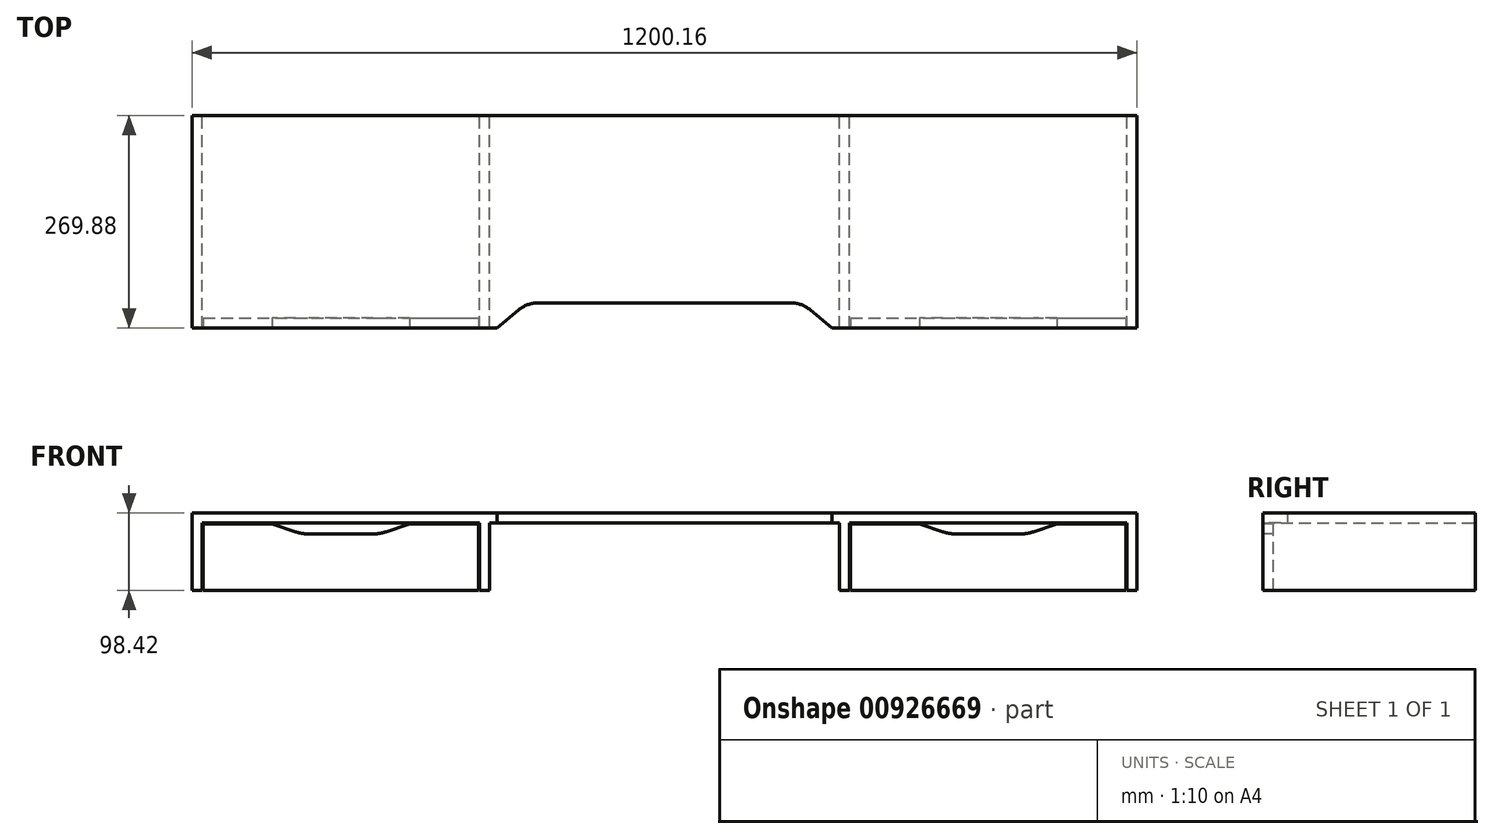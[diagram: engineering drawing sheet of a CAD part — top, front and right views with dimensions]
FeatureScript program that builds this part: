
annotation { "Feature Type Name" : "Feature", "Feature Type Description" : "" }
export const myFeature = defineFeature(function(context is Context, id is Id, definition is map)
    precondition{}
    {
        {
            var Q0;
            Q0=qCreatedBy(makeId("Top.planeOp"),FACE);
            var sketch = newSketch(context, id + "F0", { "sketchPlane" : qUnion([Q0])});
            skLineSegment(sketch, "E0.bottom", {"start": v(600.08, -134.94) * mm, "end": v(-600.08, -134.94) * mm});
            skLineSegment(sketch, "E0.top", {"start": v(600.08, 134.94) * mm, "end": v(-600.08, 134.94) * mm});
            skLineSegment(sketch, "E0.left", {"start": v(600.08, -134.94) * mm, "end": v(600.08, 134.94) * mm});
            skLineSegment(sketch, "E0.right", {"start": v(-600.08, -134.94) * mm, "end": v(-600.08, 134.94) * mm});
            skPoint(sketch, "E0.middle", {"position": v(0, 0) * mm});
            skSolve(sketch);
        }
        {
            var Q0;
            Q0 = qSketchRegion(id + "F0", true);
            extrude(context, id + "F1", {"entities" : qUnion([Q0]), "depth" : 12.7 * mm, "offsetDistance" : 25.4 * mm});
        }
        {
            var Q0;
            Q0=makeQuery(id+"F1.opExtrude","SWEPT_FACE",FACE,{"disambiguationData":[OSD([sQuery(id+"F0.wireOp",EDGE,"E0.left")])]});
            var sketch = newSketch(context, id + "F2", { "sketchPlane" : qUnion([Q0])});
            skLineSegment(sketch, "E1.bottom", {"start": v(-134.94, 0) * mm, "end": v(134.94, 0) * mm});
            skLineSegment(sketch, "E1.top", {"start": v(-134.94, -85.73) * mm, "end": v(134.94, -85.73) * mm});
            skLineSegment(sketch, "E1.left", {"start": v(-134.94, 0) * mm, "end": v(-134.94, -85.73) * mm});
            skLineSegment(sketch, "E1.right", {"start": v(134.94, 0) * mm, "end": v(134.94, -85.73) * mm});
            skSolve(sketch);
        }
        {
            var Q0;
            Q0 = qSketchRegion(id + "F2", true);
            extrude(context, id + "F3", {"entities" : qUnion([Q0]), "operationType" : NewBodyOperationType.ADD, "depth" : -12.7 * mm, "offsetDistance" : 25.4 * mm});
        }
        {
            var Q0;
            Q0=makeQuery(id+"F1.opExtrude","SWEPT_FACE",FACE,{"disambiguationData":[OSD([sQuery(id+"F0.wireOp",EDGE,"E0.right")])]});
            var sketch = newSketch(context, id + "F4", { "sketchPlane" : qUnion([Q0])});
            skLineSegment(sketch, "E2.bottom", {"start": v(-134.94, 0) * mm, "end": v(134.94, 0) * mm});
            skLineSegment(sketch, "E2.top", {"start": v(-134.94, -85.73) * mm, "end": v(134.94, -85.73) * mm});
            skLineSegment(sketch, "E2.left", {"start": v(-134.94, 0) * mm, "end": v(-134.94, -85.72) * mm});
            skLineSegment(sketch, "E2.right", {"start": v(134.94, 0) * mm, "end": v(134.94, -85.73) * mm});
            skSolve(sketch);
        }
        {
            var Q0;
            Q0 = qSketchRegion(id + "F4", true);
            extrude(context, id + "F5", {"entities" : qUnion([Q0]), "operationType" : NewBodyOperationType.ADD, "depth" : -12.7 * mm, "offsetDistance" : 25.4 * mm});
        }
        {
            var Q0;
            Q0=makeQuery(id+"F1.opExtrude","CAP_FACE",FACE,{"disambiguationData":[OSD([sQuery(id+"F0.wireOp",EDGE,"E0.bottom"),sQuery(id+"F0.wireOp",EDGE,"E0.top"),sQuery(id+"F0.wireOp",EDGE,"E0.left"),sQuery(id+"F0.wireOp",EDGE,"E0.right")])],"isStart":true});
            var sketch = newSketch(context, id + "F6", { "sketchPlane" : qUnion([Q0])});
            skLineSegment(sketch, "E3.bottom", {"start": v(222.25, 134.94) * mm, "end": v(234.95, 134.94) * mm});
            skLineSegment(sketch, "E3.top", {"start": v(222.25, -134.94) * mm, "end": v(234.95, -134.94) * mm});
            skLineSegment(sketch, "E3.left", {"start": v(222.25, 134.94) * mm, "end": v(222.25, -134.94) * mm});
            skLineSegment(sketch, "E3.right", {"start": v(234.95, 134.94) * mm, "end": v(234.95, -134.94) * mm});
            skLineSegment(sketch, "E4.bottom", {"start": v(-234.95, 134.94) * mm, "end": v(-222.25, 134.94) * mm});
            skLineSegment(sketch, "E4.top", {"start": v(-234.95, -134.94) * mm, "end": v(-222.25, -134.94) * mm});
            skLineSegment(sketch, "E4.left", {"start": v(-234.95, 134.94) * mm, "end": v(-234.95, -134.94) * mm});
            skLineSegment(sketch, "E4.right", {"start": v(-222.25, 134.94) * mm, "end": v(-222.25, -134.94) * mm});
            skSolve(sketch);
        }
        {
            var Q0;
            Q0 = qSketchRegion(id + "F6", true);
            extrude(context, id + "F7", {"entities" : qUnion([Q0]), "operationType" : NewBodyOperationType.ADD, "depth" : 85.72 * mm, "offsetDistance" : 25.4 * mm});
        }
        {
            var Q0;
            Q0=makeQuery(id+"F1.opExtrude","CAP_FACE",FACE,{"disambiguationData":[OSD([sQuery(id+"F0.wireOp",EDGE,"E0.bottom"),sQuery(id+"F0.wireOp",EDGE,"E0.top"),sQuery(id+"F0.wireOp",EDGE,"E0.left"),sQuery(id+"F0.wireOp",EDGE,"E0.right")])],"isStart":false});
            var sketch = newSketch(context, id + "F8", { "sketchPlane" : qUnion([Q0])});
            skLineSegment(sketch, "E5", {"start": v(-174.63, -103.19) * mm, "end": v(174.63, -103.19) * mm});
            skLineSegment(sketch, "E6", {"start": v(174.62, -103.19) * mm, "end": v(212.72, -134.94) * mm});
            skLineSegment(sketch, "E7", {"start": v(-174.63, -103.19) * mm, "end": v(-212.73, -134.94) * mm});
            skLineSegment(sketch, "E8", {"start": v(-212.72, -134.94) * mm, "end": v(212.73, -134.94) * mm});
            skSolve(sketch);
        }
        {
            var Q0;
            Q0=makeQuery(id+"F8.imprint","IMPRINT",FACE,{"disambiguationData":[TD([[makeQuery(id+"F8.imprint","IMPRINT",EDGE,{"derivedFrom":sQuery(id+"F8.wireOp",EDGE,"E5")}),-1.0]])]});
            extrude(context, id + "F9", {"entities" : qUnion([Q0]), "operationType" : NewBodyOperationType.REMOVE, "oppositeDirection" : true, "depth" : 12.7 * mm, "offsetDistance" : 25.4 * mm});
        }
        {
            var Q0;
            Q0=makeQuery(id+"F9.boolean.opBoolean","COPY",EDGE,{"derivedFrom":makeQuery(id+"F9.opExtrude","SWEPT_EDGE",EDGE,{"disambiguationData":[OSD([sQuery(id+"F8.wireOp",EDGE,"E5"),sQuery(id+"F8.wireOp",EDGE,"E7")])]})});
            var Q1;
            Q1=makeQuery(id+"F9.boolean.opBoolean","COPY",EDGE,{"derivedFrom":makeQuery(id+"F9.opExtrude","SWEPT_EDGE",EDGE,{"disambiguationData":[OSD([sQuery(id+"F0.wireOp",EDGE,"E0.bottom"),sQuery(id+"F8.wireOp",EDGE,"E7"),sQuery(id+"F8.wireOp",EDGE,"E8")])]})});
            var Q2;
            Q2=makeQuery(id+"F9.boolean.opBoolean","COPY",EDGE,{"derivedFrom":makeQuery(id+"F9.opExtrude","SWEPT_EDGE",EDGE,{"disambiguationData":[OSD([sQuery(id+"F8.wireOp",EDGE,"E5"),sQuery(id+"F8.wireOp",EDGE,"E6")])]})});
            var Q3;
            Q3=makeQuery(id+"F9.boolean.opBoolean","COPY",EDGE,{"derivedFrom":makeQuery(id+"F9.opExtrude","SWEPT_EDGE",EDGE,{"disambiguationData":[OSD([sQuery(id+"F0.wireOp",EDGE,"E0.bottom"),sQuery(id+"F8.wireOp",EDGE,"E6"),sQuery(id+"F8.wireOp",EDGE,"E8")])]})});
            fillet(context, id + "F10", {"entities" : qUnion([Q0, Q1, Q2, Q3]), "radius" : 38.1 * mm, "tangentPropagation" : true, "allowEdgeOverflow" : false});
        }
        {
            var Q0;
            {var subQ0=sQuery(id+"F4.wireOp",EDGE,"E2.right");var subQ4=sQuery(id+"F0.wireOp",EDGE,"E0.right");var subQ7=sQuery(id+"F0.wireOp",EDGE,"E0.bottom");var subQ10=sQuery(id+"F6.wireOp",EDGE,"E4.bottom");Q0=makeQuery(id+"F9.boolean.opBoolean","SPLIT",FACE,{"disambiguationData":[TD([makeQuery(id+"F1.opExtrude","SWEPT_FACE",FACE,{"disambiguationData":[OSD([subQ4])]})])],"derivedFrom":makeQuery(id+"F7.boolean.opBoolean","MERGE",FACE,{"derivedFrom":[makeQuery(id+"F5.boolean.opBoolean","MERGE",FACE,{"derivedFrom":[makeQuery(id+"F3.boolean.opBoolean","MERGE",FACE,{"derivedFrom":[makeQuery(id+"F1.opExtrude","SWEPT_FACE",FACE,{"disambiguationData":[OSD([subQ7])]}),makeQuery(id+"F3.opExtrude","SWEPT_FACE",FACE,{"disambiguationData":[OSD([sQuery(id+"F2.wireOp",EDGE,"E1.left")])]})]}),makeQuery(id+"F5.opExtrude","SWEPT_FACE",FACE,{"disambiguationData":[OSD([subQ0])]})]}),makeQuery(id+"F7.opExtrude","SWEPT_FACE",FACE,{"disambiguationData":[OSD([sQuery(id+"F6.wireOp",EDGE,"E3.bottom")])]}),makeQuery(id+"F7.opExtrude","SWEPT_FACE",FACE,{"disambiguationData":[OSD([subQ10])]})]})});}
            var sketch = newSketch(context, id + "F11", { "sketchPlane" : qUnion([Q0])});
            skLineSegment(sketch, "E9.bottom", {"start": v(-586.1, -1.27) * mm, "end": v(-236.22, -1.27) * mm});
            skLineSegment(sketch, "E9.top", {"start": v(-586.1, -85.73) * mm, "end": v(-236.22, -85.73) * mm});
            skLineSegment(sketch, "E9.left", {"start": v(-586.1, -1.27) * mm, "end": v(-586.1, -85.73) * mm});
            skLineSegment(sketch, "E9.right", {"start": v(-236.22, -1.27) * mm, "end": v(-236.22, -85.73) * mm});
            skSolve(sketch);
        }
        {
            var Q0;
            Q0=makeQuery(id+"F11.imprint","IMPRINT",FACE,{"disambiguationData":[TD([[makeQuery(id+"F11.imprint","IMPRINT",EDGE,{"derivedFrom":sQuery(id+"F11.wireOp",EDGE,"E9.bottom")}),-1.0]])]});
            extrude(context, id + "F12", {"entities" : qUnion([Q0]), "depth" : -12.7 * mm, "offsetDistance" : 25.4 * mm});
        }
        {
            var Q0;
            {var subQ1=sQuery(id+"F2.wireOp",EDGE,"E1.left");var subQ5=sQuery(id+"F0.wireOp",EDGE,"E0.left");var subQ7=sQuery(id+"F0.wireOp",EDGE,"E0.bottom");var subQ10=sQuery(id+"F6.wireOp",EDGE,"E3.bottom");Q0=makeQuery(id+"F9.boolean.opBoolean","SPLIT",FACE,{"disambiguationData":[TD([makeQuery(id+"F1.opExtrude","SWEPT_FACE",FACE,{"disambiguationData":[OSD([subQ5])]})])],"derivedFrom":makeQuery(id+"F7.boolean.opBoolean","MERGE",FACE,{"derivedFrom":[makeQuery(id+"F5.boolean.opBoolean","MERGE",FACE,{"derivedFrom":[makeQuery(id+"F3.boolean.opBoolean","MERGE",FACE,{"derivedFrom":[makeQuery(id+"F1.opExtrude","SWEPT_FACE",FACE,{"disambiguationData":[OSD([subQ7])]}),makeQuery(id+"F3.opExtrude","SWEPT_FACE",FACE,{"disambiguationData":[OSD([subQ1])]})]}),makeQuery(id+"F5.opExtrude","SWEPT_FACE",FACE,{"disambiguationData":[OSD([sQuery(id+"F4.wireOp",EDGE,"E2.right")])]})]}),makeQuery(id+"F7.opExtrude","SWEPT_FACE",FACE,{"disambiguationData":[OSD([subQ10])]}),makeQuery(id+"F7.opExtrude","SWEPT_FACE",FACE,{"disambiguationData":[OSD([sQuery(id+"F6.wireOp",EDGE,"E4.bottom")])]})]})});}
            var sketch = newSketch(context, id + "F13", { "sketchPlane" : qUnion([Q0])});
            skLineSegment(sketch, "E10.bottom", {"start": v(236.22, -1.27) * mm, "end": v(586.1, -1.27) * mm});
            skLineSegment(sketch, "E10.top", {"start": v(236.22, -85.73) * mm, "end": v(586.1, -85.72) * mm});
            skLineSegment(sketch, "E10.left", {"start": v(236.22, -1.27) * mm, "end": v(236.22, -85.72) * mm});
            skLineSegment(sketch, "E10.right", {"start": v(586.1, -1.27) * mm, "end": v(586.1, -85.72) * mm});
            skSolve(sketch);
        }
        {
            var Q0;
            Q0=makeQuery(id+"F13.imprint","IMPRINT",FACE,{"disambiguationData":[TD([[makeQuery(id+"F13.imprint","IMPRINT",EDGE,{"derivedFrom":sQuery(id+"F13.wireOp",EDGE,"E10.bottom")}),-1.0]])]});
            extrude(context, id + "F14", {"entities" : qUnion([Q0]), "depth" : -12.7 * mm, "offsetDistance" : 25.4 * mm});
        }
        {
            var Q0;
            Q0=makeQuery(id+"F12.opExtrude","CAP_FACE",FACE,{"disambiguationData":[OSD([sQuery(id+"F11.wireOp",EDGE,"E9.bottom"),sQuery(id+"F11.wireOp",EDGE,"E9.top"),sQuery(id+"F11.wireOp",EDGE,"E9.left"),sQuery(id+"F11.wireOp",EDGE,"E9.right")])],"isStart":true});
            var sketch = newSketch(context, id + "F15", { "sketchPlane" : qUnion([Q0])});
            skLineSegment(sketch, "E11", {"start": v(-498.63, -1.27) * mm, "end": v(-323.7, -1.27) * mm});
            skLineSegment(sketch, "E12", {"start": v(-323.7, -1.27) * mm, "end": v(-361.8, -13.97) * mm});
            skLineSegment(sketch, "E13", {"start": v(-361.8, -13.97) * mm, "end": v(-460.53, -13.97) * mm});
            skLineSegment(sketch, "E14", {"start": v(-460.53, -13.97) * mm, "end": v(-498.63, -1.27) * mm});
            skSolve(sketch);
        }
        {
            var Q0;
            Q0=makeQuery(id+"F15.imprint","IMPRINT",FACE,{"disambiguationData":[TD([[makeQuery(id+"F15.imprint","IMPRINT",EDGE,{"derivedFrom":sQuery(id+"F15.wireOp",EDGE,"E11")}),-1.0]])]});
            extrude(context, id + "F16", {"entities" : qUnion([Q0]), "operationType" : NewBodyOperationType.REMOVE, "oppositeDirection" : true, "depth" : 12.7 * mm, "offsetDistance" : 25.4 * mm});
        }
        {
            var Q0;
            Q0=makeQuery(id+"F16.boolean.opBoolean","COPY",EDGE,{"derivedFrom":makeQuery(id+"F16.opExtrude","SWEPT_EDGE",EDGE,{"disambiguationData":[OSD([sQuery(id+"F11.wireOp",EDGE,"E9.bottom"),sQuery(id+"F15.wireOp",EDGE,"E11"),sQuery(id+"F15.wireOp",EDGE,"E14")])]})});
            var Q1;
            Q1=makeQuery(id+"F16.boolean.opBoolean","COPY",EDGE,{"derivedFrom":makeQuery(id+"F16.opExtrude","SWEPT_EDGE",EDGE,{"disambiguationData":[OSD([sQuery(id+"F15.wireOp",EDGE,"E13"),sQuery(id+"F15.wireOp",EDGE,"E14")])]})});
            var Q2;
            Q2=makeQuery(id+"F16.boolean.opBoolean","COPY",EDGE,{"derivedFrom":makeQuery(id+"F16.opExtrude","SWEPT_EDGE",EDGE,{"disambiguationData":[OSD([sQuery(id+"F15.wireOp",EDGE,"E12"),sQuery(id+"F15.wireOp",EDGE,"E13")])]})});
            var Q3;
            Q3=makeQuery(id+"F16.boolean.opBoolean","COPY",EDGE,{"derivedFrom":makeQuery(id+"F16.opExtrude","SWEPT_EDGE",EDGE,{"disambiguationData":[OSD([sQuery(id+"F11.wireOp",EDGE,"E9.bottom"),sQuery(id+"F15.wireOp",EDGE,"E11"),sQuery(id+"F15.wireOp",EDGE,"E12")])]})});
            fillet(context, id + "F17", {"entities" : qUnion([Q0, Q1, Q2, Q3]), "radius" : 50.8 * mm, "tangentPropagation" : true, "allowEdgeOverflow" : false});
        }
        {
            var Q0;
            Q0=makeQuery(id+"F14.opExtrude","CAP_FACE",FACE,{"disambiguationData":[OSD([sQuery(id+"F13.wireOp",EDGE,"E10.bottom"),sQuery(id+"F13.wireOp",EDGE,"E10.top"),sQuery(id+"F13.wireOp",EDGE,"E10.left"),sQuery(id+"F13.wireOp",EDGE,"E10.right")])],"isStart":true});
            var sketch = newSketch(context, id + "F18", { "sketchPlane" : qUnion([Q0])});
            skLineSegment(sketch, "E15", {"start": v(323.7, -1.27) * mm, "end": v(498.63, -1.27) * mm});
            skLineSegment(sketch, "E16", {"start": v(498.63, -1.27) * mm, "end": v(460.53, -13.97) * mm});
            skLineSegment(sketch, "E17", {"start": v(460.53, -13.97) * mm, "end": v(361.8, -13.97) * mm});
            skLineSegment(sketch, "E18", {"start": v(361.8, -13.97) * mm, "end": v(323.7, -1.27) * mm});
            skSolve(sketch);
        }
        {
            var Q0;
            Q0=makeQuery(id+"F18.imprint","IMPRINT",FACE,{"disambiguationData":[TD([[makeQuery(id+"F18.imprint","IMPRINT",EDGE,{"derivedFrom":sQuery(id+"F18.wireOp",EDGE,"E15")}),-1.0]])]});
            extrude(context, id + "F19", {"entities" : qUnion([Q0]), "operationType" : NewBodyOperationType.REMOVE, "oppositeDirection" : true, "depth" : 12.7 * mm, "offsetDistance" : 25.4 * mm});
        }
        {
            var Q0;
            Q0=makeQuery(id+"F19.boolean.opBoolean","COPY",EDGE,{"derivedFrom":makeQuery(id+"F19.opExtrude","SWEPT_EDGE",EDGE,{"disambiguationData":[OSD([sQuery(id+"F13.wireOp",EDGE,"E10.bottom"),sQuery(id+"F18.wireOp",EDGE,"E15"),sQuery(id+"F18.wireOp",EDGE,"E18")])]})});
            var Q1;
            Q1=makeQuery(id+"F19.boolean.opBoolean","COPY",EDGE,{"derivedFrom":makeQuery(id+"F19.opExtrude","SWEPT_EDGE",EDGE,{"disambiguationData":[OSD([sQuery(id+"F18.wireOp",EDGE,"E17"),sQuery(id+"F18.wireOp",EDGE,"E18")])]})});
            var Q2;
            Q2=makeQuery(id+"F19.boolean.opBoolean","COPY",EDGE,{"derivedFrom":makeQuery(id+"F19.opExtrude","SWEPT_EDGE",EDGE,{"disambiguationData":[OSD([sQuery(id+"F18.wireOp",EDGE,"E16"),sQuery(id+"F18.wireOp",EDGE,"E17")])]})});
            var Q3;
            Q3=makeQuery(id+"F19.boolean.opBoolean","COPY",EDGE,{"derivedFrom":makeQuery(id+"F19.opExtrude","SWEPT_EDGE",EDGE,{"disambiguationData":[OSD([sQuery(id+"F13.wireOp",EDGE,"E10.bottom"),sQuery(id+"F18.wireOp",EDGE,"E15"),sQuery(id+"F18.wireOp",EDGE,"E16")])]})});
            fillet(context, id + "F20", {"entities" : qUnion([Q0, Q1, Q2, Q3]), "radius" : 50.8 * mm, "tangentPropagation" : true, "allowEdgeOverflow" : false});
        }
    });
